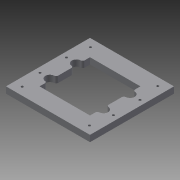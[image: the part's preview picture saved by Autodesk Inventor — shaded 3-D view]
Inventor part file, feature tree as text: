
AUTODESK INVENTOR PART (.ipt)
format: ipt  version: 2014 SP1 (Build 180222100, 222)  size: 109,056 bytes
history: native  units: in
note: dims shown in document units (in); Inventor stores cm internally (conversion verified against a paired STEP export)
features: extrude x1, sketch x1
ambient origin geometry x8: Origin, YZ Plane, XZ Plane, XY Plane, X Axis, Y Axis, Z Axis, Center Point
bodies: Solid1 (feature_tree)
feature tree (2):
  extrude  "Extrusion1"  [1 undecoded]
  sketch  "Sketch1"  dims[d0=0.1875in d1=0.0in]
note: 1 required parameter value undecoded (feature->parameter linkage not recoverable at this tier; creation-order binding heuristic only, values carry confidence <= 0.55)
